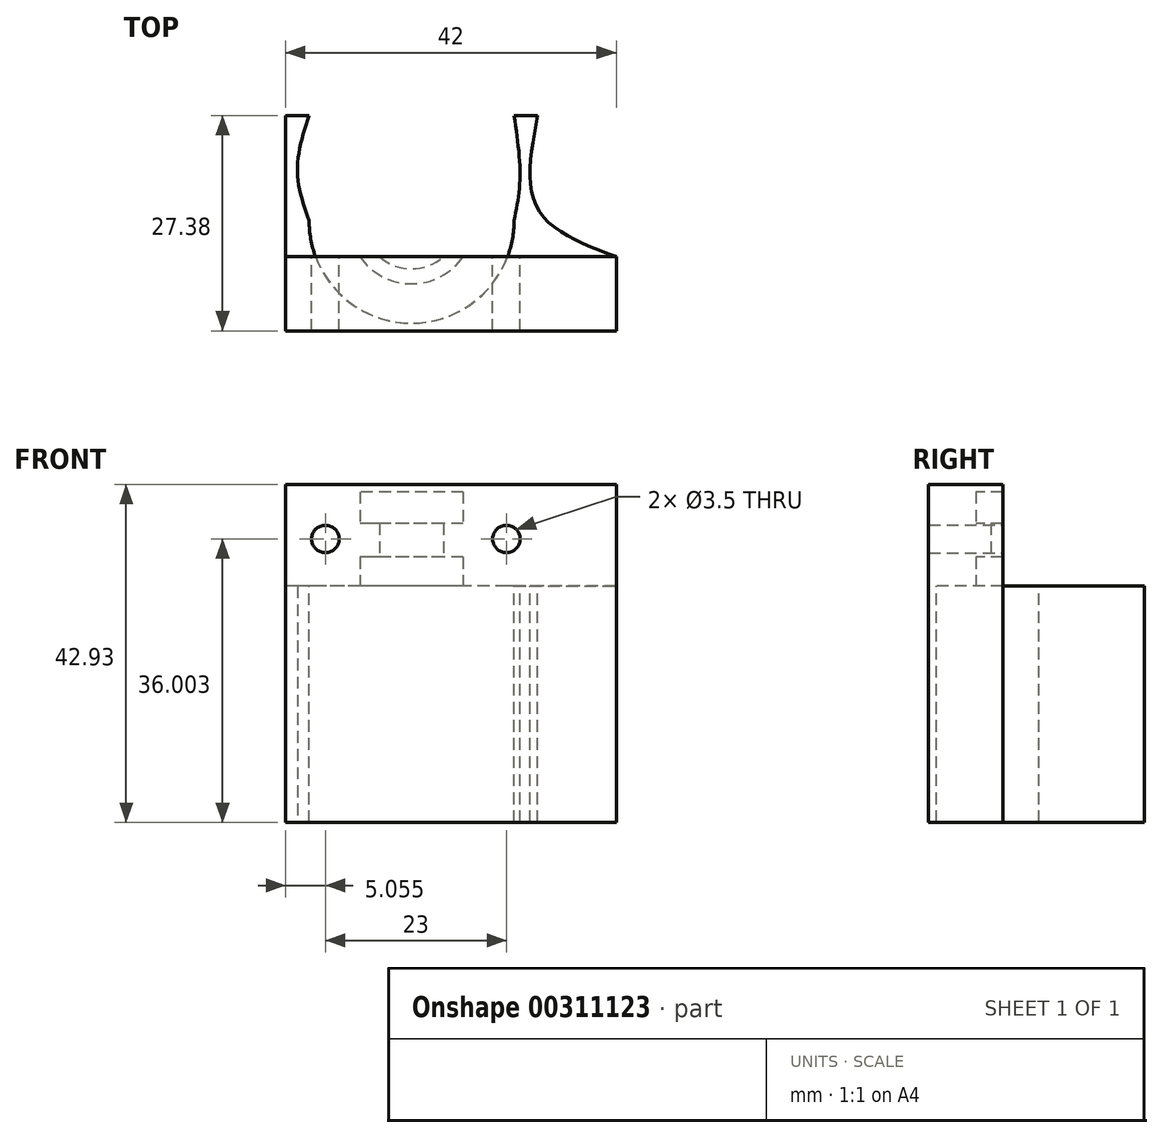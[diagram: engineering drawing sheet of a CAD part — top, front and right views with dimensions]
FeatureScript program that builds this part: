
annotation { "Feature Type Name" : "Feature", "Feature Type Description" : "" }
export const myFeature = defineFeature(function(context is Context, id is Id, definition is map)
    precondition{}
    {
        {
            var Q0;
            Q0=qCreatedBy(makeId("Front.planeOp"),FACE);
            var sketch = newSketch(context, id + "F0", { "sketchPlane" : qUnion([Q0])});
            skLineSegment(sketch, "E0.bottom", {"start": v(-15.61, 5.48) * mm, "end": v(17.39, 5.48) * mm});
            skLineSegment(sketch, "E0.top", {"start": v(-15.61, -7.45) * mm, "end": v(17.39, -7.45) * mm});
            skLineSegment(sketch, "E0.left", {"start": v(-15.61, 5.48) * mm, "end": v(-15.61, -7.45) * mm});
            skLineSegment(sketch, "E0.right", {"start": v(17.39, 5.48) * mm, "end": v(17.39, -7.45) * mm});
            skCircle(sketch, "E1", {"center": v(-10.56, -1.45) * mm, "radius": 1.75 * mm});
            skCircle(sketch, "E2", {"center": v(12.44, -1.45) * mm, "radius": 1.75 * mm});
            skSolve(sketch);
        }
        {
            var Q0;
            Q0 = qSketchRegion(id + "F0", true);
            extrude(context, id + "F1", {"entities" : qUnion([Q0]), "depth" : 20 * mm});
        }
        {
            var Q0;
            Q0=makeQuery(id+"F1.opExtrude","SWEPT_FACE",FACE,{"disambiguationData":[OSD([sQuery(id+"F0.wireOp",EDGE,"E0.top"),sQuery(id+"F0.wireOp",EDGE,"05a502c3-fa31-4569-8b68-3abbb8395af1.bottom")])]});
            var sketch = newSketch(context, id + "F2", { "sketchPlane" : qUnion([Q0])});
            skPoint(sketch, "E3.endSnap0", {"position": v(0.39, 5.54) * mm});
            skCircle(sketch, "E4", {"center": v(0.39, 10) * mm, "radius": 8 * mm});
            skSolve(sketch);
        }
        {
            var Q0;
            Q0 = qSketchRegion(id + "F2", true);
            extrude(context, id + "F3", {"entities" : qUnion([Q0]), "operationType" : NewBodyOperationType.REMOVE, "oppositeDirection" : true, "depth" : 12 * mm});
        }
        {
            var Q0;
            Q0=makeQuery(id+"F1.opExtrude","SWEPT_FACE",FACE,{"disambiguationData":[OSD([sQuery(id+"F0.wireOp",EDGE,"E0.top")])]});
            var sketch = newSketch(context, id + "F4", { "sketchPlane" : qUnion([Q0])});
            skCircle(sketch, "E5", {"center": v(0.39, 10) * mm, "radius": 8 * mm});
            skSolve(sketch);
        }
        {
            var Q0;
            Q0 = qSketchRegion(id + "F4", true);
            extrude(context, id + "F5", {"entities" : qUnion([Q0]), "operationType" : NewBodyOperationType.ADD, "oppositeDirection" : true, "depth" : 8 * mm});
        }
        {
            var Q0;
            Q0=makeQuery(id+"F5.boolean.opBoolean","MERGE",FACE,{"derivedFrom":[makeQuery(id+"F1.opExtrude","SWEPT_FACE",FACE,{"disambiguationData":[OSD([sQuery(id+"F0.wireOp",EDGE,"E0.top")])]}),makeQuery(id+"F5.opExtrude","CAP_FACE",FACE,{"disambiguationData":[OSD([sQuery(id+"F4.wireOp",EDGE,"E5")])],"isStart":true})]});
            var sketch = newSketch(context, id + "F6", { "sketchPlane" : qUnion([Q0])});
            skLineSegment(sketch, "E6", {"start": v(-15.61, 10) * mm, "end": v(0.39, 10) * mm, "construction": true});
            skPoint(sketch, "E6.endSnap0", {"position": v(-15.61, 10) * mm});
            skLineSegment(sketch, "E7", {"start": v(0.39, 10) * mm, "end": v(0.39, 20) * mm, "construction": true});
            skCircle(sketch, "E8", {"center": v(0.39, 10) * mm, "radius": 6.1 * mm});
            skSolve(sketch);
        }
        {
            var Q0;
            Q0=makeQuery(id+"F6.imprint","IMPRINT",FACE,{"disambiguationData":[TD([[makeQuery(id+"F6.imprint","IMPRINT",EDGE,{"derivedFrom":sQuery(id+"F6.wireOp",EDGE,"E8")}),1.0]])]});
            var Q1;
            Q1=sQuery(id+"F6.wireOp",EDGE,"E8");
            extrude(context, id + "F7", {"entities" : qUnion([Q0]), "operationType" : NewBodyOperationType.REMOVE, "surfaceEntities" : qUnion([Q1]), "oppositeDirection" : true, "depth" : 8 * mm});
        }
        {
            var Q0;
            Q0=makeQuery(id+"F5.boolean.opBoolean","MERGE",FACE,{"derivedFrom":[makeQuery(id+"F1.opExtrude","SWEPT_FACE",FACE,{"disambiguationData":[OSD([sQuery(id+"F0.wireOp",EDGE,"E0.top")])]}),makeQuery(id+"F5.opExtrude","CAP_FACE",FACE,{"disambiguationData":[OSD([sQuery(id+"F4.wireOp",EDGE,"E5")])],"isStart":true})]});
            var sketch = newSketch(context, id + "F8", { "sketchPlane" : qUnion([Q0])});
            skCircle(sketch, "E9", {"center": v(0.39, 10) * mm, "radius": 8 * mm});
            skSolve(sketch);
        }
        {
            var Q0;
            Q0 = qSketchRegion(id + "F8", true);
            extrude(context, id + "F9", {"entities" : qUnion([Q0]), "operationType" : NewBodyOperationType.REMOVE, "oppositeDirection" : true, "depth" : 3.7 * mm});
        }
        {
            var Q0;
            Q0=makeQuery(id+"F5.boolean.opBoolean","MERGE",FACE,{"derivedFrom":[makeQuery(id+"F1.opExtrude","SWEPT_FACE",FACE,{"disambiguationData":[OSD([sQuery(id+"F0.wireOp",EDGE,"E0.top")])]}),makeQuery(id+"F5.opExtrude","CAP_FACE",FACE,{"disambiguationData":[OSD([sQuery(id+"F4.wireOp",EDGE,"E5")])],"isStart":true})]});
            var sketch = newSketch(context, id + "F10", { "sketchPlane" : qUnion([Q0])});
            skLineSegment(sketch, "E10.bottom", {"start": v(-15.61, 20) * mm, "end": v(17.39, 20) * mm});
            skLineSegment(sketch, "E10.top", {"start": v(-15.61, 14.5) * mm, "end": v(17.39, 14.5) * mm});
            skLineSegment(sketch, "E10.left", {"start": v(-15.61, 20) * mm, "end": v(-15.61, 14.5) * mm});
            skLineSegment(sketch, "E10.right", {"start": v(17.39, 20) * mm, "end": v(17.39, 14.5) * mm});
            skSolve(sketch);
        }
        {
            var Q0;
            {var subQ0=sQuery(id+"F0.wireOp",EDGE,"E0.top");var subQ1=makeQuery(id+"F1.opExtrude","CAP_EDGE",EDGE,{"disambiguationData":[OSD([subQ0])],"isStart":true});Q0=makeQuery(id+"F10.imprint","IMPRINT",FACE,{"disambiguationData":[TD([[makeQuery(id+"F10.imprint","IMPRINT",EDGE,{"derivedFrom":subQ1}),1.0]])]});}
            var sketch = newSketch(context, id + "F11", { "sketchPlane" : qUnion([Q0])});
            skLineSegment(sketch, "E11.top", {"start": v(18.07, 14.57) * mm, "end": v(-16.93, 14.57) * mm});
            skLineSegment(sketch, "E11.left", {"start": v(18.07, 0) * mm, "end": v(18.07, 14.57) * mm});
            skLineSegment(sketch, "E11.right", {"start": v(-16.93, 0) * mm, "end": v(-16.93, 14.57) * mm});
            skLineSegment(sketch, "E12", {"start": v(-16.93, 0) * mm, "end": v(-16.93, -2.27) * mm});
            skLineSegment(sketch, "E13", {"start": v(-16.93, -2.27) * mm, "end": v(18.07, -2.27) * mm});
            skLineSegment(sketch, "E14", {"start": v(18.07, -2.27) * mm, "end": v(18.07, 0) * mm});
            skSolve(sketch);
        }
        {
            var Q0;
            Q0 = qSketchRegion(id + "F11", true);
            extrude(context, id + "F12", {"entities" : qUnion([Q0]), "operationType" : NewBodyOperationType.REMOVE, "oppositeDirection" : true, "depth" : 25 * mm});
        }
        {
            var Q0;
            Q0=makeQuery(id+"F1.opExtrude","CAP_FACE",FACE,{"disambiguationData":[OSD([sQuery(id+"F0.wireOp",EDGE,"E0.bottom"),sQuery(id+"F0.wireOp",EDGE,"E0.top"),sQuery(id+"F0.wireOp",EDGE,"E0.left"),sQuery(id+"F0.wireOp",EDGE,"E0.right"),sQuery(id+"F0.wireOp",EDGE,"E1"),sQuery(id+"F0.wireOp",EDGE,"E2")])],"isStart":false});
            extrude(context, id + "F13", {"entities" : qUnion([Q0]), "operationType" : NewBodyOperationType.ADD, "depth" : 4 * mm});
        }
        {
            var Q0;
            {var subQ0=sQuery(id+"F0.wireOp",EDGE,"E0.right");Q0=makeQuery(id+"F13.boolean.opBoolean","MERGE",FACE,{"derivedFrom":[makeQuery(id+"F1.opExtrude","SWEPT_FACE",FACE,{"disambiguationData":[OSD([subQ0])]}),makeQuery(id+"F13.opExtrude","SWEPT_FACE",FACE,{"disambiguationData":[OSD([subQ0])]})]});}
            extrude(context, id + "F14", {"entities" : qUnion([Q0]), "operationType" : NewBodyOperationType.ADD, "depth" : 9 * mm});
        }
        {
            var Q0;
            {var subQ0=sQuery(id+"F0.wireOp",EDGE,"E0.top");Q0=makeQuery(id+"F14.boolean.opBoolean","MERGE",FACE,{"derivedFrom":[makeQuery(id+"F13.boolean.opBoolean","MERGE",FACE,{"derivedFrom":[makeQuery(id+"F5.boolean.opBoolean","MERGE",FACE,{"derivedFrom":[makeQuery(id+"F1.opExtrude","SWEPT_FACE",FACE,{"disambiguationData":[OSD([subQ0])]}),makeQuery(id+"F5.opExtrude","CAP_FACE",FACE,{"disambiguationData":[OSD([sQuery(id+"F4.wireOp",EDGE,"E5")])],"isStart":true})]}),makeQuery(id+"F13.opExtrude","SWEPT_FACE",FACE,{"disambiguationData":[OSD([subQ0])]})]}),makeQuery(id+"F14.opExtrude","SWEPT_FACE",FACE,{"disambiguationData":[OSD([subQ0,sQuery(id+"F0.wireOp",EDGE,"E0.right")])]})]});}
            var sketch = newSketch(context, id + "F15", { "sketchPlane" : qUnion([Q0])});
            skArc(sketch, "E15", {"start": v(13.4, 10) * mm, "mid": v(0.39, 23.02) * mm, "end": v(-12.63, 10) * mm});
            skLineSegment(sketch, "E16", {"start": v(-15.61, 14.57) * mm, "end": v(-15.61, -3.38) * mm});
            skLineSegment(sketch, "E17", {"start": v(-12.63, -3.38) * mm, "end": v(-15.61, -3.38) * mm});
            skLineSegment(sketch, "E18", {"start": v(13.4, -3.38) * mm, "end": v(16.4, -3.38) * mm});
            skFitSpline(sketch, "E19", {"points": [v(16.4, -3.38) * mm, v(16.4, 8.47) * mm, v(26.39, 14.57) * mm], "startDerivative": vector(-5.02, 26.47) * mm, "endDerivative": vector(25.02, 9.4) * mm});
            skFitSpline(sketch, "E20", {"points": [v(-12.63, 10) * mm, v(-14.12, 3.6) * mm, v(-12.63, -3.38) * mm], "startDerivative": vector(-4.5, -12.92) * mm, "endDerivative": vector(4.44, -13.84) * mm});
            skFitSpline(sketch, "E21", {"points": [v(13.4, 10) * mm, v(14.17, 4.46) * mm, v(13.4, -3.38) * mm], "startDerivative": vector(2.36, -11.58) * mm, "endDerivative": vector(-2.23, -15.08) * mm});
            skLineSegment(sketch, "E22", {"start": v(-15.61, 14.57) * mm, "end": v(-15.61, 24) * mm});
            skLineSegment(sketch, "E23", {"start": v(-15.61, 24) * mm, "end": v(26.39, 24) * mm});
            skLineSegment(sketch, "E24", {"start": v(26.39, 24) * mm, "end": v(26.39, 14.57) * mm});
            skSolve(sketch);
        }
        {
            var Q0;
            Q0 = qSketchRegion(id + "F15", true);
            extrude(context, id + "F16", {"entities" : qUnion([Q0]), "operationType" : NewBodyOperationType.ADD, "depth" : 30 * mm});
        }
    });
